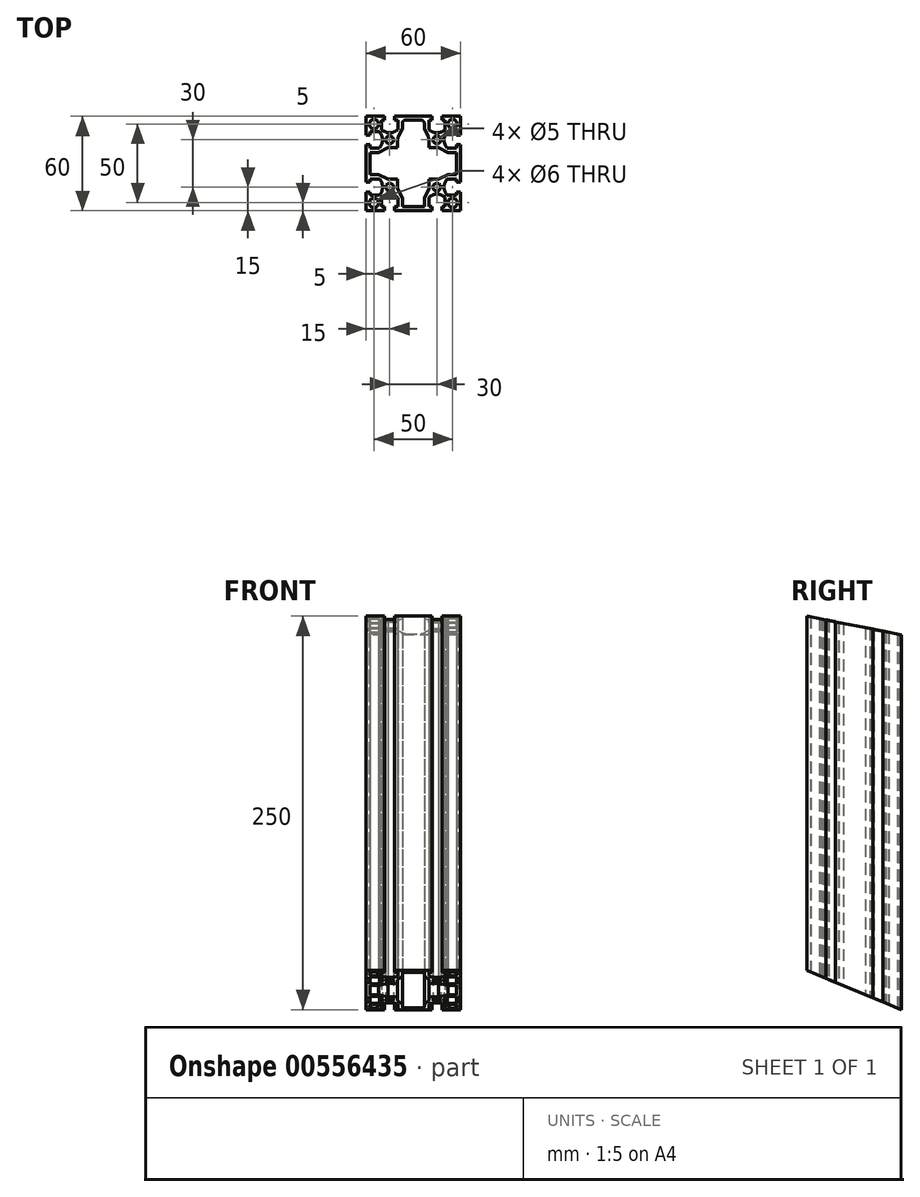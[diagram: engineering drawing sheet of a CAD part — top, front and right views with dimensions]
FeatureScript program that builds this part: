
annotation { "Feature Type Name" : "Feature", "Feature Type Description" : "" }
export const myFeature = defineFeature(function(context is Context, id is Id, definition is map)
    precondition{}
    {
        {
            var Q0;
            Q0=qCreatedBy(makeId("Top.planeOp"),FACE);
            var sketch = newSketch(context, id + "F0", { "sketchPlane" : qUnion([Q0])});
            skLineSegment(sketch, "E0.bottom", {"start": v(30, -30) * mm, "end": v(-30, -30) * mm});
            skLineSegment(sketch, "E0.top", {"start": v(30, 30) * mm, "end": v(-30, 30) * mm});
            skLineSegment(sketch, "E0.left", {"start": v(30, -30) * mm, "end": v(30, 30) * mm});
            skLineSegment(sketch, "E0.right", {"start": v(-30, -30) * mm, "end": v(-30, 30) * mm});
            skPoint(sketch, "E0.middle", {"position": v(0, 0) * mm});
            skLineSegment(sketch, "E1.top", {"start": v(-11.85, 30) * mm, "end": v(-18.15, 30) * mm});
            skLineSegment(sketch, "E1.left", {"start": v(-11.85, 27.5) * mm, "end": v(-11.85, 30) * mm});
            skLineSegment(sketch, "E1.right", {"start": v(-18.15, 27.5) * mm, "end": v(-18.15, 30) * mm});
            skPoint(sketch, "E1.middle", {"position": v(-15, 28.75) * mm});
            skLineSegment(sketch, "E2.bottom", {"start": v(-9.85, 27.5) * mm, "end": v(-11.85, 27.5) * mm});
            skLineSegment(sketch, "E2.left", {"start": v(-9.85, 27.5) * mm, "end": v(-9.85, 21.55) * mm});
            skLineSegment(sketch, "E2.right", {"start": v(-20.15, 27.5) * mm, "end": v(-20.15, 21.55) * mm});
            skPoint(sketch, "E2.middle", {"position": v(-15, 24.52) * mm});
            skArc(sketch, "E3", {"start": v(-20.15, 21.55) * mm, "mid": v(-15, 19.5) * mm, "end": v(-9.85, 21.55) * mm});
            skPoint(sketch, "E4.MirrorP", {"position": v(15, 24.52) * mm});
            skPoint(sketch, "E5.MirrorP", {"position": v(15, 28.75) * mm});
            skLineSegment(sketch, "E6.MirrorCS", {"start": v(11.85, 27.5) * mm, "end": v(11.85, 30) * mm});
            skLineSegment(sketch, "E7.MirrorCS", {"start": v(18.15, 27.5) * mm, "end": v(18.15, 30) * mm});
            skLineSegment(sketch, "E8.MirrorCS", {"start": v(9.85, 27.5) * mm, "end": v(11.85, 27.5) * mm});
            skLineSegment(sketch, "E9.MirrorCS", {"start": v(9.85, 27.5) * mm, "end": v(9.85, 21.55) * mm});
            skArc(sketch, "E10.MirrorCS", {"start": v(20.15, 21.55) * mm, "mid": v(15, 19.5) * mm, "end": v(9.85, 21.55) * mm});
            skLineSegment(sketch, "E11.MirrorCS", {"start": v(20.15, 27.5) * mm, "end": v(20.15, 21.55) * mm});
            skLineSegment(sketch, "E12.MirrorCS", {"start": v(11.85, 30) * mm, "end": v(18.15, 30) * mm});
            skLineSegment(sketch, "E13.1.0", {"start": v(27.5, 20.15) * mm, "end": v(21.55, 20.15) * mm});
            skLineSegment(sketch, "E13.1.1", {"start": v(27.5, 9.85) * mm, "end": v(21.55, 9.85) * mm});
            skArc(sketch, "E13.1.2", {"start": v(21.55, 20.15) * mm, "mid": v(19.5, 15) * mm, "end": v(21.55, 9.85) * mm});
            skLineSegment(sketch, "E13.1.3", {"start": v(27.5, -9.85) * mm, "end": v(21.55, -9.85) * mm});
            skLineSegment(sketch, "E13.1.4", {"start": v(27.5, -20.15) * mm, "end": v(21.55, -20.15) * mm});
            skPoint(sketch, "E13.1.5", {"position": v(28.75, 15) * mm});
            skPoint(sketch, "E13.1.6", {"position": v(28.75, -15) * mm});
            skArc(sketch, "E13.1.7", {"start": v(21.55, -20.15) * mm, "mid": v(19.5, -15) * mm, "end": v(21.55, -9.85) * mm});
            skPoint(sketch, "E13.1.8", {"position": v(24.52, -15) * mm});
            skPoint(sketch, "E13.1.9", {"position": v(24.52, 15) * mm});
            skLineSegment(sketch, "E13.1.10", {"start": v(27.5, 9.85) * mm, "end": v(27.5, 20.15) * mm});
            skLineSegment(sketch, "E13.1.11", {"start": v(27.5, -11.85) * mm, "end": v(27.5, -18.15) * mm});
            skLineSegment(sketch, "E13.1.12", {"start": v(30, 11.85) * mm, "end": v(30, 18.15) * mm});
            skLineSegment(sketch, "E13.1.13", {"start": v(30, -11.85) * mm, "end": v(30, -18.15) * mm});
            skLineSegment(sketch, "E13.1.14", {"start": v(27.5, 18.15) * mm, "end": v(30, 18.15) * mm});
            skLineSegment(sketch, "E13.1.15", {"start": v(27.5, 11.85) * mm, "end": v(30, 11.85) * mm});
            skLineSegment(sketch, "E13.1.16", {"start": v(27.5, 11.85) * mm, "end": v(27.5, 18.15) * mm});
            skLineSegment(sketch, "E13.1.17", {"start": v(27.5, -9.85) * mm, "end": v(27.5, -20.15) * mm});
            skLineSegment(sketch, "E13.1.18", {"start": v(27.5, -18.15) * mm, "end": v(30, -18.15) * mm});
            skLineSegment(sketch, "E13.1.19", {"start": v(27.5, -11.85) * mm, "end": v(30, -11.85) * mm});
            skLineSegment(sketch, "E13.2.0", {"start": v(20.15, -27.5) * mm, "end": v(20.15, -21.55) * mm});
            skLineSegment(sketch, "E13.2.1", {"start": v(9.85, -27.5) * mm, "end": v(9.85, -21.55) * mm});
            skArc(sketch, "E13.2.2", {"start": v(20.15, -21.55) * mm, "mid": v(15, -19.5) * mm, "end": v(9.85, -21.55) * mm});
            skLineSegment(sketch, "E13.2.3", {"start": v(-9.85, -27.5) * mm, "end": v(-9.85, -21.55) * mm});
            skLineSegment(sketch, "E13.2.4", {"start": v(-20.15, -27.5) * mm, "end": v(-20.15, -21.55) * mm});
            skPoint(sketch, "E13.2.5", {"position": v(15, -28.75) * mm});
            skPoint(sketch, "E13.2.6", {"position": v(-15, -28.75) * mm});
            skArc(sketch, "E13.2.7", {"start": v(-20.15, -21.55) * mm, "mid": v(-15, -19.5) * mm, "end": v(-9.85, -21.55) * mm});
            skPoint(sketch, "E13.2.8", {"position": v(-15, -24.52) * mm});
            skPoint(sketch, "E13.2.9", {"position": v(15, -24.52) * mm});
            skLineSegment(sketch, "E13.2.10", {"start": v(9.85, -27.5) * mm, "end": v(20.15, -27.5) * mm});
            skLineSegment(sketch, "E13.2.11", {"start": v(-11.85, -27.5) * mm, "end": v(-18.15, -27.5) * mm});
            skLineSegment(sketch, "E13.2.12", {"start": v(11.85, -30) * mm, "end": v(18.15, -30) * mm});
            skLineSegment(sketch, "E13.2.13", {"start": v(-11.85, -30) * mm, "end": v(-18.15, -30) * mm});
            skLineSegment(sketch, "E13.2.14", {"start": v(18.15, -27.5) * mm, "end": v(18.15, -30) * mm});
            skLineSegment(sketch, "E13.2.15", {"start": v(11.85, -27.5) * mm, "end": v(11.85, -30) * mm});
            skLineSegment(sketch, "E13.2.16", {"start": v(11.85, -27.5) * mm, "end": v(18.15, -27.5) * mm});
            skLineSegment(sketch, "E13.2.17", {"start": v(-9.85, -27.5) * mm, "end": v(-20.15, -27.5) * mm});
            skLineSegment(sketch, "E13.2.18", {"start": v(-18.15, -27.5) * mm, "end": v(-18.15, -30) * mm});
            skLineSegment(sketch, "E13.2.19", {"start": v(-11.85, -27.5) * mm, "end": v(-11.85, -30) * mm});
            skLineSegment(sketch, "E13.3.0", {"start": v(-27.5, -20.15) * mm, "end": v(-21.55, -20.15) * mm});
            skLineSegment(sketch, "E13.3.1", {"start": v(-27.5, -9.85) * mm, "end": v(-21.55, -9.85) * mm});
            skArc(sketch, "E13.3.2", {"start": v(-21.55, -20.15) * mm, "mid": v(-19.5, -15) * mm, "end": v(-21.55, -9.85) * mm});
            skLineSegment(sketch, "E13.3.3", {"start": v(-27.5, 9.85) * mm, "end": v(-21.55, 9.85) * mm});
            skLineSegment(sketch, "E13.3.4", {"start": v(-27.5, 20.15) * mm, "end": v(-21.55, 20.15) * mm});
            skPoint(sketch, "E13.3.5", {"position": v(-28.75, -15) * mm});
            skPoint(sketch, "E13.3.6", {"position": v(-28.75, 15) * mm});
            skArc(sketch, "E13.3.7", {"start": v(-21.55, 20.15) * mm, "mid": v(-19.5, 15) * mm, "end": v(-21.55, 9.85) * mm});
            skPoint(sketch, "E13.3.8", {"position": v(-24.52, 15) * mm});
            skPoint(sketch, "E13.3.9", {"position": v(-24.52, -15) * mm});
            skLineSegment(sketch, "E13.3.10", {"start": v(-27.5, -9.85) * mm, "end": v(-27.5, -20.15) * mm});
            skLineSegment(sketch, "E13.3.11", {"start": v(-27.5, 11.85) * mm, "end": v(-27.5, 18.15) * mm});
            skLineSegment(sketch, "E13.3.12", {"start": v(-30, -11.85) * mm, "end": v(-30, -18.15) * mm});
            skLineSegment(sketch, "E13.3.13", {"start": v(-30, 11.85) * mm, "end": v(-30, 18.15) * mm});
            skLineSegment(sketch, "E13.3.14", {"start": v(-27.5, -18.15) * mm, "end": v(-30, -18.15) * mm});
            skLineSegment(sketch, "E13.3.15", {"start": v(-27.5, -11.85) * mm, "end": v(-30, -11.85) * mm});
            skLineSegment(sketch, "E13.3.16", {"start": v(-27.5, -11.85) * mm, "end": v(-27.5, -18.15) * mm});
            skLineSegment(sketch, "E13.3.17", {"start": v(-27.5, 9.85) * mm, "end": v(-27.5, 20.15) * mm});
            skLineSegment(sketch, "E13.3.18", {"start": v(-27.5, 18.15) * mm, "end": v(-30, 18.15) * mm});
            skLineSegment(sketch, "E13.3.19", {"start": v(-27.5, 11.85) * mm, "end": v(-30, 11.85) * mm});
            skLineSegment(sketch, "E13.anchor1", {"start": v(0, 0) * mm, "end": v(-20.15, 21.55) * mm, "construction": true});
            skLineSegment(sketch, "E13.anchor2", {"start": v(0, 0) * mm, "end": v(-21.55, -20.15) * mm, "construction": true});
            skLineSegment(sketch, "E14.trimOffspring", {"start": v(-18.15, 27.5) * mm, "end": v(-20.15, 27.5) * mm});
            skLineSegment(sketch, "E15.trimOffspring", {"start": v(18.15, 27.5) * mm, "end": v(20.15, 27.5) * mm});
            skCircle(sketch, "E16", {"center": v(-15, 15) * mm, "radius": 2.5 * mm});
            skCircle(sketch, "E17", {"center": v(-25, 25) * mm, "radius": 3 * mm});
            skCircle(sketch, "E18.MirrorC", {"center": v(25, 25) * mm, "radius": 3 * mm});
            skCircle(sketch, "E19.MirrorC", {"center": v(25, -25) * mm, "radius": 3 * mm});
            skCircle(sketch, "E20.MirrorC", {"center": v(-25, -25) * mm, "radius": 3 * mm});
            skCircle(sketch, "E21.MirrorC", {"center": v(15, 15) * mm, "radius": 2.5 * mm});
            skCircle(sketch, "E22.MirrorC", {"center": v(15, -15) * mm, "radius": 2.5 * mm});
            skCircle(sketch, "E23.MirrorC", {"center": v(-15, -15) * mm, "radius": 2.5 * mm});
            skLineSegment(sketch, "E24", {"start": v(-7, 27.5) * mm, "end": v(0, 27.5) * mm});
            skLineSegment(sketch, "E25", {"start": v(-7, 27.5) * mm, "end": v(-7, 22) * mm});
            skLineSegment(sketch, "E26", {"start": v(-10, 10) * mm, "end": v(-10, 16) * mm});
            skLineSegment(sketch, "E27", {"start": v(-10, 16) * mm, "end": v(-7, 22) * mm});
            skLineSegment(sketch, "E28.MirrorCS", {"start": v(10, 10) * mm, "end": v(10, 16) * mm});
            skLineSegment(sketch, "E29.MirrorCS", {"start": v(10, 16) * mm, "end": v(7, 22) * mm});
            skLineSegment(sketch, "E30.MirrorCS", {"start": v(7, 27.5) * mm, "end": v(0, 27.5) * mm});
            skLineSegment(sketch, "E31.MirrorCS", {"start": v(7, 27.5) * mm, "end": v(7, 22) * mm});
            skLineSegment(sketch, "E32.1.0", {"start": v(-10, -10) * mm, "end": v(-16, -10) * mm});
            skLineSegment(sketch, "E32.1.1", {"start": v(-16, -10) * mm, "end": v(-22, -7) * mm});
            skLineSegment(sketch, "E32.1.2", {"start": v(-27.5, -7) * mm, "end": v(-22, -7) * mm});
            skLineSegment(sketch, "E32.1.3", {"start": v(-27.5, -7) * mm, "end": v(-27.5, 0) * mm});
            skLineSegment(sketch, "E32.1.4", {"start": v(-27.5, 7) * mm, "end": v(-27.5, 0) * mm});
            skLineSegment(sketch, "E32.1.5", {"start": v(-27.5, 7) * mm, "end": v(-22, 7) * mm});
            skLineSegment(sketch, "E32.1.6", {"start": v(-16, 10) * mm, "end": v(-22, 7) * mm});
            skLineSegment(sketch, "E32.1.7", {"start": v(-10, 10) * mm, "end": v(-16, 10) * mm});
            skLineSegment(sketch, "E32.2.0", {"start": v(10, -10) * mm, "end": v(10, -16) * mm});
            skLineSegment(sketch, "E32.2.1", {"start": v(10, -16) * mm, "end": v(7, -22) * mm});
            skLineSegment(sketch, "E32.2.2", {"start": v(7, -27.5) * mm, "end": v(7, -22) * mm});
            skLineSegment(sketch, "E32.2.3", {"start": v(7, -27.5) * mm, "end": v(0, -27.5) * mm});
            skLineSegment(sketch, "E32.2.4", {"start": v(-7, -27.5) * mm, "end": v(0, -27.5) * mm});
            skLineSegment(sketch, "E32.2.5", {"start": v(-7, -27.5) * mm, "end": v(-7, -22) * mm});
            skLineSegment(sketch, "E32.2.6", {"start": v(-10, -16) * mm, "end": v(-7, -22) * mm});
            skLineSegment(sketch, "E32.2.7", {"start": v(-10, -10) * mm, "end": v(-10, -16) * mm});
            skLineSegment(sketch, "E32.3.0", {"start": v(10, 10) * mm, "end": v(16, 10) * mm});
            skLineSegment(sketch, "E32.3.1", {"start": v(16, 10) * mm, "end": v(22, 7) * mm});
            skLineSegment(sketch, "E32.3.2", {"start": v(27.5, 7) * mm, "end": v(22, 7) * mm});
            skLineSegment(sketch, "E32.3.3", {"start": v(27.5, 7) * mm, "end": v(27.5, 0) * mm});
            skLineSegment(sketch, "E32.3.4", {"start": v(27.5, -7) * mm, "end": v(27.5, 0) * mm});
            skLineSegment(sketch, "E32.3.5", {"start": v(27.5, -7) * mm, "end": v(22, -7) * mm});
            skLineSegment(sketch, "E32.3.6", {"start": v(16, -10) * mm, "end": v(22, -7) * mm});
            skLineSegment(sketch, "E32.3.7", {"start": v(10, -10) * mm, "end": v(16, -10) * mm});
            skSolve(sketch);
        }
        {
            var Q0;
            {var subQ30=sQuery(id+"F0.wireOp",EDGE,"E1.left");Q0=makeQuery(id+"F0.imprint","IMPRINT",FACE,{"disambiguationData":[TD([[makeQuery(id+"F0.imprint","IMPRINT",EDGE,{"derivedFrom":subQ30}),-1.0]])]});}
            extrude(context, id + "F1", {"entities" : qUnion([Q0]), "depth" : 250 * mm, "offsetDistance" : 25 * mm});
        }
        {
            var Q0;
            Q0=makeQuery(id+"F1.opExtrude","SWEPT_EDGE",EDGE,{"disambiguationData":[OSD([sQuery(id+"F0.wireOp",EDGE,"E24"),sQuery(id+"F0.wireOp",EDGE,"E25")])]});
            var Q1;
            Q1=makeQuery(id+"F1.opExtrude","SWEPT_EDGE",EDGE,{"disambiguationData":[OSD([sQuery(id+"F0.wireOp",EDGE,"E30.MirrorCS"),sQuery(id+"F0.wireOp",EDGE,"E31.MirrorCS")])]});
            var Q2;
            Q2=makeQuery(id+"F1.opExtrude","SWEPT_EDGE",EDGE,{"disambiguationData":[OSD([sQuery(id+"F0.wireOp",EDGE,"840db5bc-c403-45cd-90c7-254e62d9e8c5.3.2"),sQuery(id+"F0.wireOp",EDGE,"840db5bc-c403-45cd-90c7-254e62d9e8c5.3.3")])]});
            var Q3;
            Q3=makeQuery(id+"F1.opExtrude","SWEPT_EDGE",EDGE,{"disambiguationData":[OSD([sQuery(id+"F0.wireOp",EDGE,"840db5bc-c403-45cd-90c7-254e62d9e8c5.3.4"),sQuery(id+"F0.wireOp",EDGE,"840db5bc-c403-45cd-90c7-254e62d9e8c5.3.5")])]});
            var Q4;
            Q4=makeQuery(id+"F1.opExtrude","SWEPT_EDGE",EDGE,{"disambiguationData":[OSD([sQuery(id+"F0.wireOp",EDGE,"840db5bc-c403-45cd-90c7-254e62d9e8c5.1.4"),sQuery(id+"F0.wireOp",EDGE,"840db5bc-c403-45cd-90c7-254e62d9e8c5.1.5")])]});
            var Q5;
            Q5=makeQuery(id+"F1.opExtrude","SWEPT_EDGE",EDGE,{"disambiguationData":[OSD([sQuery(id+"F0.wireOp",EDGE,"840db5bc-c403-45cd-90c7-254e62d9e8c5.1.2"),sQuery(id+"F0.wireOp",EDGE,"840db5bc-c403-45cd-90c7-254e62d9e8c5.1.3")])]});
            var Q6;
            Q6=makeQuery(id+"F1.opExtrude","SWEPT_EDGE",EDGE,{"disambiguationData":[OSD([sQuery(id+"F0.wireOp",EDGE,"840db5bc-c403-45cd-90c7-254e62d9e8c5.2.2"),sQuery(id+"F0.wireOp",EDGE,"840db5bc-c403-45cd-90c7-254e62d9e8c5.2.3")])]});
            var Q7;
            Q7=makeQuery(id+"F1.opExtrude","SWEPT_EDGE",EDGE,{"disambiguationData":[OSD([sQuery(id+"F0.wireOp",EDGE,"840db5bc-c403-45cd-90c7-254e62d9e8c5.2.4"),sQuery(id+"F0.wireOp",EDGE,"840db5bc-c403-45cd-90c7-254e62d9e8c5.2.5")])]});
            fillet(context, id + "F2", {"entities" : qUnion([Q0, Q1, Q2, Q3, Q4, Q5, Q6, Q7]), "radius" : 2 * mm, "tangentPropagation" : true, "allowEdgeOverflow" : false});
        }
        {
            var Q0;
            Q0=makeQuery(id+"F1.opExtrude","SWEPT_EDGE",EDGE,{"disambiguationData":[OSD([sQuery(id+"F0.wireOp",EDGE,"E26"),sQuery(id+"F0.wireOp",EDGE,"E27")])]});
            var Q1;
            Q1=makeQuery(id+"F1.opExtrude","SWEPT_EDGE",EDGE,{"disambiguationData":[OSD([sQuery(id+"F0.wireOp",EDGE,"E28.MirrorCS"),sQuery(id+"F0.wireOp",EDGE,"E29.MirrorCS")])]});
            var Q2;
            Q2=makeQuery(id+"F1.opExtrude","SWEPT_EDGE",EDGE,{"disambiguationData":[OSD([sQuery(id+"F0.wireOp",EDGE,"840db5bc-c403-45cd-90c7-254e62d9e8c5.3.0"),sQuery(id+"F0.wireOp",EDGE,"840db5bc-c403-45cd-90c7-254e62d9e8c5.3.1")])]});
            var Q3;
            Q3=makeQuery(id+"F1.opExtrude","SWEPT_EDGE",EDGE,{"disambiguationData":[OSD([sQuery(id+"F0.wireOp",EDGE,"840db5bc-c403-45cd-90c7-254e62d9e8c5.1.6"),sQuery(id+"F0.wireOp",EDGE,"840db5bc-c403-45cd-90c7-254e62d9e8c5.1.7")])]});
            var Q4;
            Q4=makeQuery(id+"F1.opExtrude","SWEPT_EDGE",EDGE,{"disambiguationData":[OSD([sQuery(id+"F0.wireOp",EDGE,"840db5bc-c403-45cd-90c7-254e62d9e8c5.1.0"),sQuery(id+"F0.wireOp",EDGE,"840db5bc-c403-45cd-90c7-254e62d9e8c5.1.1")])]});
            var Q5;
            Q5=makeQuery(id+"F1.opExtrude","SWEPT_EDGE",EDGE,{"disambiguationData":[OSD([sQuery(id+"F0.wireOp",EDGE,"840db5bc-c403-45cd-90c7-254e62d9e8c5.3.6"),sQuery(id+"F0.wireOp",EDGE,"840db5bc-c403-45cd-90c7-254e62d9e8c5.3.7")])]});
            var Q6;
            Q6=makeQuery(id+"F1.opExtrude","SWEPT_EDGE",EDGE,{"disambiguationData":[OSD([sQuery(id+"F0.wireOp",EDGE,"840db5bc-c403-45cd-90c7-254e62d9e8c5.2.0"),sQuery(id+"F0.wireOp",EDGE,"840db5bc-c403-45cd-90c7-254e62d9e8c5.2.1")])]});
            var Q7;
            Q7=makeQuery(id+"F1.opExtrude","SWEPT_EDGE",EDGE,{"disambiguationData":[OSD([sQuery(id+"F0.wireOp",EDGE,"840db5bc-c403-45cd-90c7-254e62d9e8c5.2.6"),sQuery(id+"F0.wireOp",EDGE,"840db5bc-c403-45cd-90c7-254e62d9e8c5.2.7")])]});
            fillet(context, id + "F3", {"entities" : qUnion([Q0, Q1, Q2, Q3, Q4, Q5, Q6, Q7]), "radius" : 7 * mm, "tangentPropagation" : true, "allowEdgeOverflow" : false});
        }
        {
            var Q0;
            Q0=qCreatedBy(makeId("Right.planeOp"),FACE);
            var sketch = newSketch(context, id + "F4", { "sketchPlane" : qUnion([Q0])});
            skLineSegment(sketch, "E33.bottom", {"start": v(30, 0) * mm, "end": v(-168.53, 82.23) * mm});
            skLineSegment(sketch, "E33.top", {"start": v(-23.26, -128.57) * mm, "end": v(-221.79, -46.34) * mm});
            skLineSegment(sketch, "E33.left", {"start": v(30, 0) * mm, "end": v(-23.26, -128.57) * mm});
            skLineSegment(sketch, "E33.right", {"start": v(-168.53, 82.23) * mm, "end": v(-221.79, -46.34) * mm});
            skLineSegment(sketch, "E34.bottom", {"start": v(-8, 360.56) * mm, "end": v(-30, 250) * mm});
            skLineSegment(sketch, "E34.top", {"start": v(171.75, 324.8) * mm, "end": v(149.76, 214.24) * mm});
            skLineSegment(sketch, "E34.left", {"start": v(-8, 360.56) * mm, "end": v(171.75, 324.8) * mm});
            skLineSegment(sketch, "E34.right", {"start": v(-30, 250) * mm, "end": v(149.76, 214.24) * mm});
            skSolve(sketch);
        }
        {
            var Q0;
            Q0=qSketchRegion(id+"F4",true);
            extrude(context, id + "F5", {"entities" : qUnion([Q0]), "operationType" : NewBodyOperationType.REMOVE, "depth" : 30 * mm, "offsetDistance" : 25 * mm, "hasSecondDirection" : true, "secondDirectionOppositeDirection" : true, "secondDirectionDepth" : 30 * mm});
        }
    });
